# Revit family: Runtal-EB3-120D-120-Volts-36
name_source: partatom
category: Mechanical Equipment
units: mm (PartAtom-declared; Revit-internal decimal feet)

## family parameters
Classification Number = 23.75.10.14.14
Cut with Voids When Loaded = No
Host = Face
Maintain Annotation Orientation = No
Part Type = Normal
Room Calculation Point = No
Round Connector Dimension = Use Diameter
Shared = No

## types (1)
- Electric Baseboard-EB3-120D-36-Runtal-Commercial
    Assembly Code = D3020
    Casing = Powder Coated-Runtal-W-White
    Default Elevation = 1219.2 mm  [stored 4 ft]
    Description = 36" Runtal’s electric baseboard combines high outputs and low surface temperatures with the fine design and outstanding outputs.
    Grille = Yes
    Lamelle = Yes
    Logo = Paint-Runtal-B-Black Matte
    Manufacturer = Runtal Radiators
    Model = EB3-120D-(120 Volts)-36
    URL = http://www.runtalnorthamerica.com
    Vertical Conection = Powder Coated-Runtal- Brass

note: [stored X ft] marks values corroborated as IEEE doubles in the binary element streams (Revit-internal decimal feet)

## geometry (parser evidence)
native form markers: Blend x22, Sweep x7
no freeform markers — native parametric forms only
